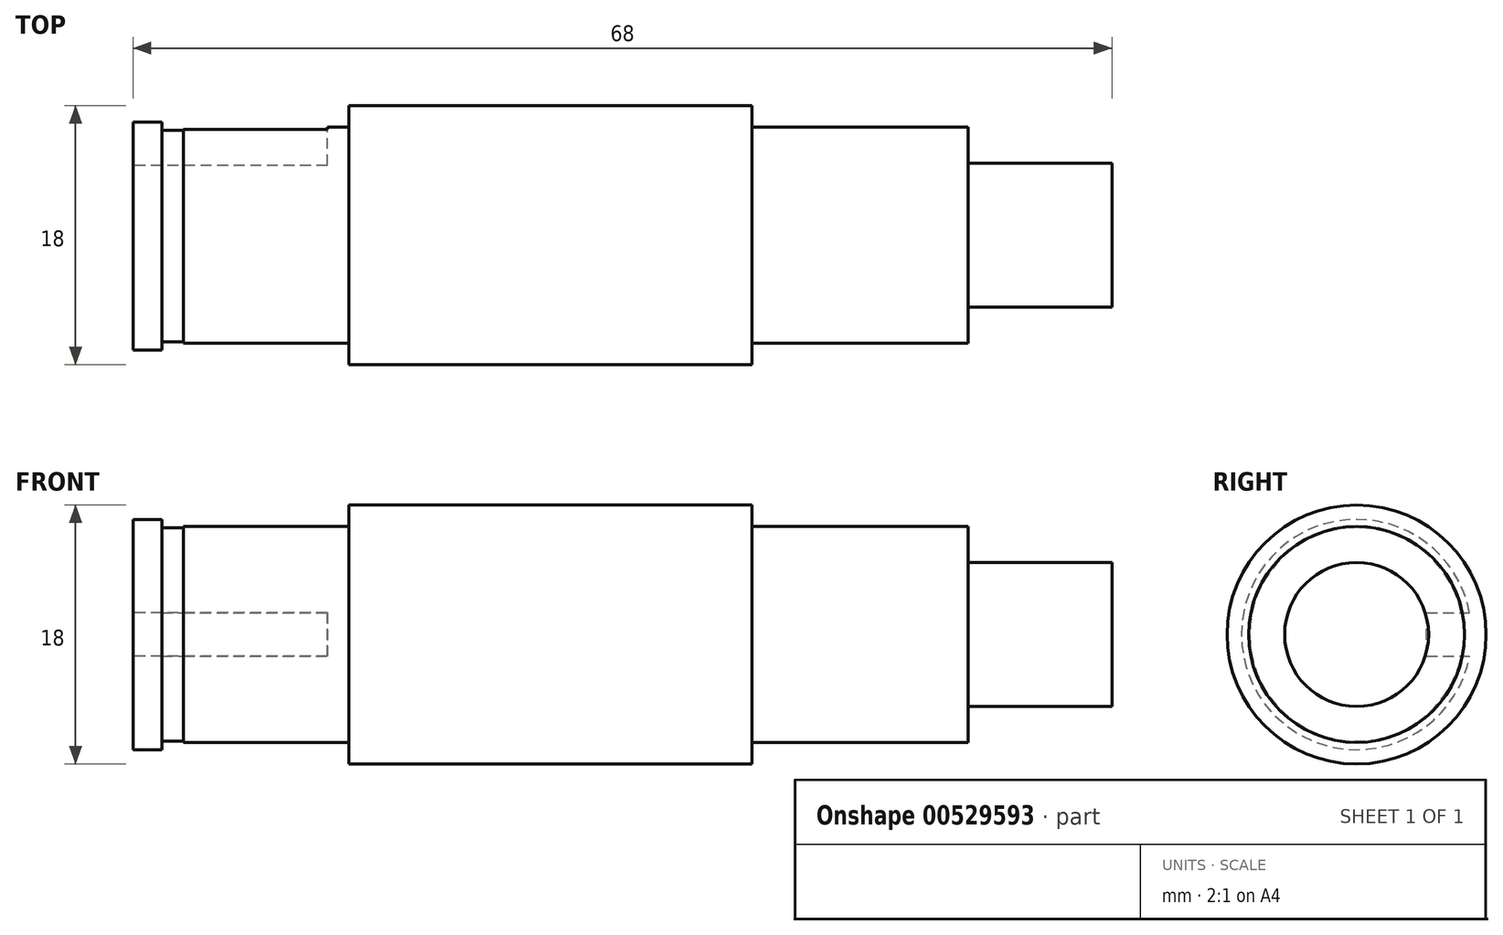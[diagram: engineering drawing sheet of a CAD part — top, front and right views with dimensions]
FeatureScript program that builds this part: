
annotation { "Feature Type Name" : "Feature", "Feature Type Description" : "" }
export const myFeature = defineFeature(function(context is Context, id is Id, definition is map)
    precondition{}
    {
        {
            var Q0;
            Q0=qCreatedBy(makeId("Right.planeOp"),FACE);
            var sketch = newSketch(context, id + "F0", { "sketchPlane" : qUnion([Q0])});
            skCircle(sketch, "E0", {"center": v(0, 0) * mm, "radius": 9 * mm});
            skSolve(sketch);
        }
        {
            var Q0;
            Q0 = qSketchRegion(id + "F0", true);
            extrude(context, id + "F1", {"entities" : qUnion([Q0]), "endBound" : BoundingType.SYMMETRIC, "depth" : 28 * mm, "offsetDistance" : 25 * mm});
        }
        {
            var Q0;
            Q0=makeQuery(id+"F1.opExtrude","CAP_FACE",FACE,{"disambiguationData":[OSD([sQuery(id+"F0.wireOp",EDGE,"E0")])],"isStart":false});
            var sketch = newSketch(context, id + "F2", { "sketchPlane" : qUnion([Q0])});
            skCircle(sketch, "E1", {"center": v(0, 0) * mm, "radius": 7.5 * mm});
            skSolve(sketch);
        }
        {
            var Q0;
            Q0 = qSketchRegion(id + "F2", true);
            extrude(context, id + "F3", {"entities" : qUnion([Q0]), "operationType" : NewBodyOperationType.ADD, "depth" : 15 * mm, "offsetDistance" : 25 * mm});
        }
        {
            var Q0;
            Q0=makeQuery(id+"F3.opExtrude","CAP_FACE",FACE,{"disambiguationData":[OSD([sQuery(id+"F2.wireOp",EDGE,"E1")])],"isStart":false});
            var sketch = newSketch(context, id + "F4", { "sketchPlane" : qUnion([Q0])});
            skCircle(sketch, "E2", {"center": v(0, 0) * mm, "radius": 5 * mm});
            skSolve(sketch);
        }
        {
            var Q0;
            Q0 = qSketchRegion(id + "F4", true);
            extrude(context, id + "F5", {"entities" : qUnion([Q0]), "operationType" : NewBodyOperationType.ADD, "depth" : 10 * mm, "offsetDistance" : 25 * mm});
        }
        {
            var Q0;
            Q0=makeQuery(id+"F1.opExtrude","CAP_FACE",FACE,{"disambiguationData":[OSD([sQuery(id+"F0.wireOp",EDGE,"E0")])],"isStart":true});
            var sketch = newSketch(context, id + "F6", { "sketchPlane" : qUnion([Q0])});
            skCircle(sketch, "E3", {"center": v(0, 0) * mm, "radius": 7.5 * mm});
            skSolve(sketch);
        }
        {
            var Q0;
            Q0 = qSketchRegion(id + "F6", true);
            extrude(context, id + "F7", {"entities" : qUnion([Q0]), "operationType" : NewBodyOperationType.ADD, "depth" : (15 - 3.5) * mm, "offsetDistance" : 25 * mm});
        }
        {
            var Q0;
            Q0=makeQuery(id+"F7.opExtrude","CAP_FACE",FACE,{"disambiguationData":[OSD([sQuery(id+"F6.wireOp",EDGE,"E3")])],"isStart":false});
            var sketch = newSketch(context, id + "F8", { "sketchPlane" : qUnion([Q0])});
            skCircle(sketch, "E4", {"center": v(0, 0) * mm, "radius": 7.42 * mm});
            skSolve(sketch);
        }
        {
            var Q0;
            Q0 = qSketchRegion(id + "F8", true);
            extrude(context, id + "F9", {"entities" : qUnion([Q0]), "operationType" : NewBodyOperationType.ADD, "depth" : 1.5 * mm, "offsetDistance" : 25 * mm});
        }
        {
            var Q0;
            Q0=makeQuery(id+"F9.opExtrude","CAP_FACE",FACE,{"disambiguationData":[OSD([sQuery(id+"F8.wireOp",EDGE,"E4")])],"isStart":false});
            var sketch = newSketch(context, id + "F10", { "sketchPlane" : qUnion([Q0])});
            skCircle(sketch, "E5", {"center": v(0, 0) * mm, "radius": 8 * mm});
            skSolve(sketch);
        }
        {
            var Q0;
            Q0 = qSketchRegion(id + "F10", true);
            extrude(context, id + "F11", {"entities" : qUnion([Q0]), "operationType" : NewBodyOperationType.ADD, "depth" : (3.5 - 1.5) * mm, "offsetDistance" : 25 * mm});
        }
        {
            var Q0;
            Q0=makeQuery(id+"F11.opExtrude","CAP_FACE",FACE,{"disambiguationData":[OSD([sQuery(id+"F10.wireOp",EDGE,"E5")])],"isStart":false});
            var sketch = newSketch(context, id + "F12", { "sketchPlane" : qUnion([Q0])});
            skLineSegment(sketch, "E6.bottom", {"start": v(-4.86, -1.5) * mm, "end": v(-7.86, -1.5) * mm});
            skLineSegment(sketch, "E6.top", {"start": v(-4.86, 1.5) * mm, "end": v(-7.86, 1.5) * mm});
            skLineSegment(sketch, "E6.left", {"start": v(-4.86, -1.5) * mm, "end": v(-4.86, 1.5) * mm});
            skPoint(sketch, "E6.middle", {"position": v(-6.36, 0) * mm});
            skPoint(sketch, "E7.1.internal.orphan", {"position": v(-8, 0) * mm});
            skFitSpline(sketch, "E8", {"points": [v(-7.86, 1.5) * mm, v(-8.25, 0) * mm, v(-7.86, -1.5) * mm], "startDerivative": vector(-1.18, -3) * mm, "endDerivative": vector(1.18, -3) * mm});
            skSolve(sketch);
        }
        {
            var Q0;
            Q0 = qSketchRegion(id + "F12", true);
            extrude(context, id + "F13", {"entities" : qUnion([Q0]), "operationType" : NewBodyOperationType.REMOVE, "oppositeDirection" : true, "depth" : 13.5 * mm, "offsetDistance" : 25 * mm});
        }
    });
